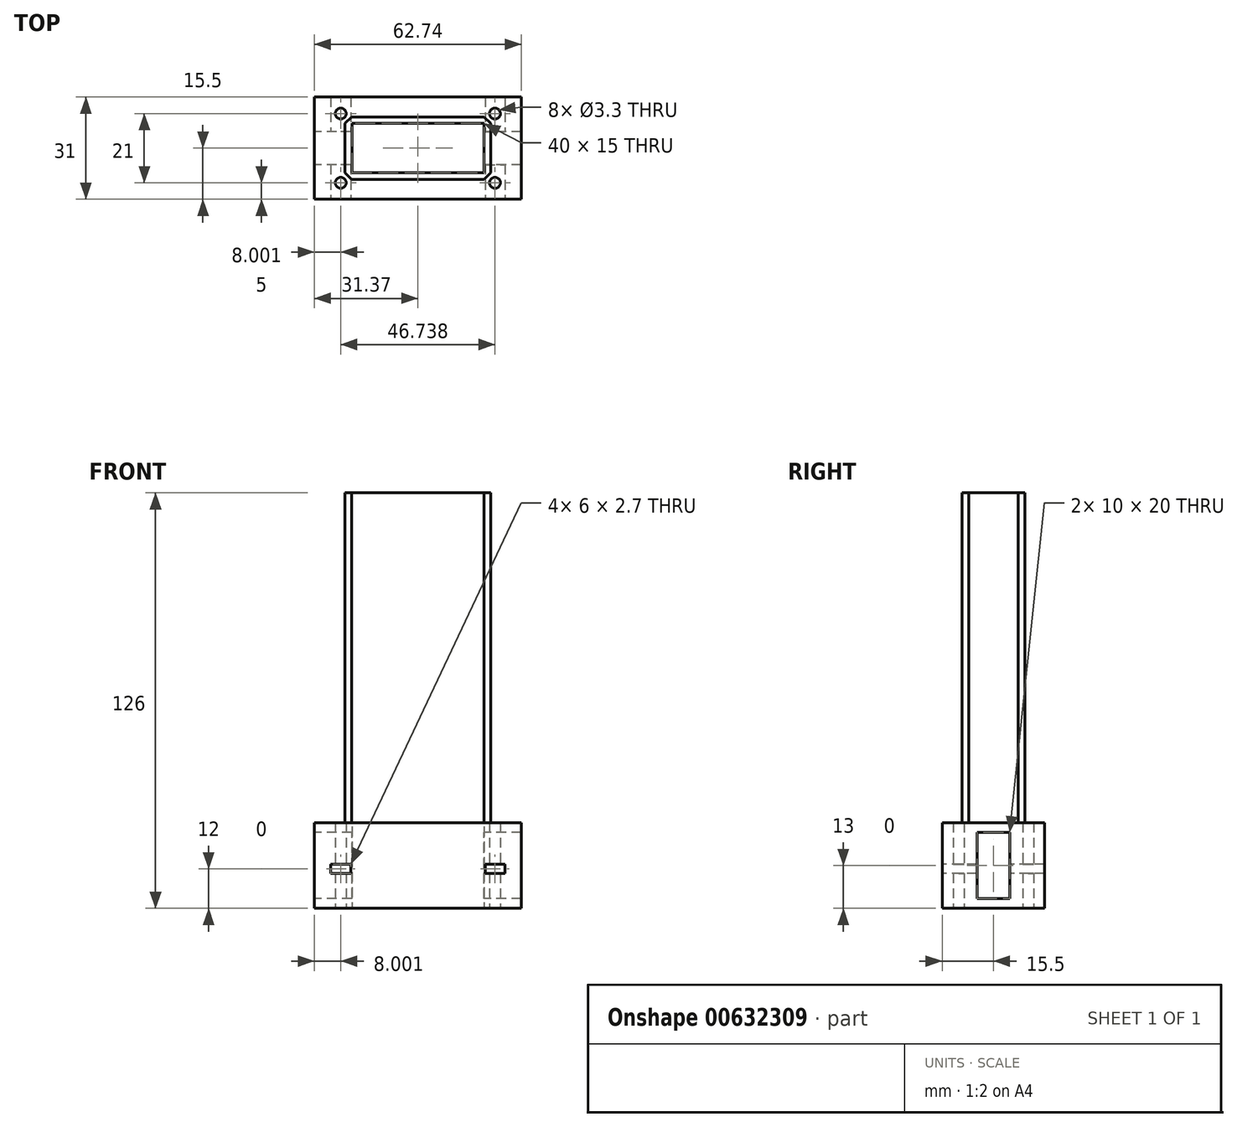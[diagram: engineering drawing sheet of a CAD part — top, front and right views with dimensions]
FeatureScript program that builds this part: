
annotation { "Feature Type Name" : "Feature", "Feature Type Description" : "" }
export const myFeature = defineFeature(function(context is Context, id is Id, definition is map)
    precondition{}
    {
        {
            var Q0;
            Q0=qCreatedBy(makeId("Top.planeOp"),FACE);
            var sketch = newSketch(context, id + "F0", { "sketchPlane" : qUnion([Q0])});
            skLineSegment(sketch, "E0.bottom", {"start": v(31.37, 15.5) * mm, "end": v(-31.37, 15.5) * mm});
            skLineSegment(sketch, "E0.top", {"start": v(31.37, -15.5) * mm, "end": v(-31.37, -15.5) * mm});
            skLineSegment(sketch, "E0.left", {"start": v(31.37, 15.5) * mm, "end": v(31.37, -15.5) * mm});
            skLineSegment(sketch, "E0.right", {"start": v(-31.37, 15.5) * mm, "end": v(-31.37, -15.5) * mm});
            skPoint(sketch, "E0.middle", {"position": v(0, 0) * mm});
            skLineSegment(sketch, "E1.bottom", {"start": v(23.37, -10.5) * mm, "end": v(-23.37, -10.5) * mm, "construction": true});
            skLineSegment(sketch, "E1.top", {"start": v(23.37, 10.5) * mm, "end": v(-23.37, 10.5) * mm, "construction": true});
            skLineSegment(sketch, "E1.left", {"start": v(23.37, -10.5) * mm, "end": v(23.37, 10.5) * mm, "construction": true});
            skLineSegment(sketch, "E1.right", {"start": v(-23.37, -10.5) * mm, "end": v(-23.37, 10.5) * mm, "construction": true});
            skLineSegment(sketch, "E2.bottom", {"start": v(20, -7.5) * mm, "end": v(-20, -7.5) * mm});
            skLineSegment(sketch, "E2.top", {"start": v(20, 7.5) * mm, "end": v(-20, 7.5) * mm});
            skLineSegment(sketch, "E2.left", {"start": v(20, -7.5) * mm, "end": v(20, 7.5) * mm});
            skLineSegment(sketch, "E2.right", {"start": v(-20, -7.5) * mm, "end": v(-20, 7.5) * mm});
            skPoint(sketch, "E3", {"position": v(-23.37, 10.5) * mm});
            skPoint(sketch, "E4", {"position": v(-23.37, -10.5) * mm});
            skPoint(sketch, "E5", {"position": v(23.37, -10.5) * mm});
            skPoint(sketch, "E6", {"position": v(23.37, 10.5) * mm});
            skSolve(sketch);
        }
        {
            var Q0;
            Q0 = qSketchRegion(id + "F0", true);
            extrude(context, id + "F1", {"entities" : qUnion([Q0]), "depth" : 26 * mm, "offsetDistance" : 25 * mm});
        }
        {
            var Q0;
            Q0=makeQuery(id+"F1.opExtrude","SWEPT_FACE",FACE,{"disambiguationData":[OSD([sQuery(id+"F0.wireOp",EDGE,"E0.right")])]});
            var sketch = newSketch(context, id + "F2", { "sketchPlane" : qUnion([Q0])});
            skLineSegment(sketch, "E7.bottom", {"start": v(5, 3) * mm, "end": v(-5, 3) * mm});
            skLineSegment(sketch, "E7.top", {"start": v(5, 23) * mm, "end": v(-5, 23) * mm});
            skLineSegment(sketch, "E7.left", {"start": v(5, 3) * mm, "end": v(5, 23) * mm});
            skLineSegment(sketch, "E7.right", {"start": v(-5, 3) * mm, "end": v(-5, 23) * mm});
            skPoint(sketch, "E7.middle", {"position": v(0, 13) * mm});
            skSolve(sketch);
        }
        {
            var Q0;
            Q0=makeQuery(id+"F2.imprint","IMPRINT",FACE,{"disambiguationData":[TD([[makeQuery(id+"F2.imprint","IMPRINT",EDGE,{"derivedFrom":sQuery(id+"F2.wireOp",EDGE,"E7.bottom")}),-1.0]])]});
            extrude(context, id + "F3", {"entities" : qUnion([Q0]), "operationType" : NewBodyOperationType.REMOVE, "endBound" : BoundingType.THROUGH_ALL, "oppositeDirection" : true, "depth" : 25 * mm, "offsetDistance" : 25 * mm});
        }
        {
            var Q0;
            Q0=sQuery(id+"F0.wireOp",VERTEX,"E3");
            var Q1;
            Q1=sQuery(id+"F0.wireOp",VERTEX,"E4");
            var Q2;
            Q2=sQuery(id+"F0.wireOp",VERTEX,"E5");
            var Q3;
            Q3=sQuery(id+"F0.wireOp",VERTEX,"E6");
            var Q4;
            Q4=makeQuery(id+"F1.opExtrude","SWEPT_BODY",BODY,{"disambiguationData":[OSD([sQuery(id+"F0.wireOp",EDGE,"E0.bottom"),sQuery(id+"F0.wireOp",EDGE,"E0.top"),sQuery(id+"F0.wireOp",EDGE,"E0.left"),sQuery(id+"F0.wireOp",EDGE,"E0.right"),sQuery(id+"F0.wireOp",EDGE,"E2.bottom"),sQuery(id+"F0.wireOp",EDGE,"E2.top"),sQuery(id+"F0.wireOp",EDGE,"E2.left"),sQuery(id+"F0.wireOp",EDGE,"E2.right")])]});
            hole(context, id + "F4", {"style" : HoleStyle.SIMPLE, "endStyle" : HoleEndStyle.THROUGH, "oppositeDirection" : true, "standardTappedOrClearance" : lookupTablePath({ "standard" : "ISO", "fit" : "Normal", "size" : "M3", "type" : "Clearance" }), "standardBlindInLast" : lookupTablePath({ "fit" : "Standard", "standard" : "ISO", "size" : "M3", "type" : "Clearance" }), "holeDiameter" : 3.3 * mm, "majorDiameter" : 5 * mm, "isTappedThrough" : true, "tappedDepth" : 12 * mm, "tapClearance" : 3, "locations" : qUnion([Q0, Q1, Q2, Q3]), "scope" : qUnion([Q4])});
        }
        {
            var Q0;
            Q0=makeQuery(id+"F1.opExtrude","CAP_FACE",FACE,{"disambiguationData":[OSD([sQuery(id+"F0.wireOp",EDGE,"E0.bottom"),sQuery(id+"F0.wireOp",EDGE,"E0.top"),sQuery(id+"F0.wireOp",EDGE,"E0.left"),sQuery(id+"F0.wireOp",EDGE,"E0.right"),sQuery(id+"F0.wireOp",EDGE,"E2.bottom"),sQuery(id+"F0.wireOp",EDGE,"E2.top"),sQuery(id+"F0.wireOp",EDGE,"E2.left"),sQuery(id+"F0.wireOp",EDGE,"E2.right")])],"isStart":false});
            var sketch = newSketch(context, id + "F5", { "sketchPlane" : qUnion([Q0])});
            skLineSegment(sketch, "E8.bottom", {"start": v(-22.06, -9.5) * mm, "end": v(22.06, -9.5) * mm});
            skLineSegment(sketch, "E8.top", {"start": v(-22.06, 9.5) * mm, "end": v(22.06, 9.5) * mm});
            skLineSegment(sketch, "E8.left", {"start": v(-22.06, -9.5) * mm, "end": v(-22.06, 9.5) * mm});
            skLineSegment(sketch, "E8.right", {"start": v(22.06, -9.5) * mm, "end": v(22.06, 9.5) * mm});
            skPoint(sketch, "E8.middle", {"position": v(0, 0) * mm});
            skSolve(sketch);
        }
        {
            var Q0;
            Q0=makeQuery(id+"F5.imprint","IMPRINT",FACE,{"disambiguationData":[TD([[makeQuery(id+"F5.imprint","IMPRINT",EDGE,{"derivedFrom":sQuery(id+"F5.wireOp",EDGE,"E8.bottom")}),1.0]])]});
            extrude(context, id + "F6", {"entities" : qUnion([Q0]), "operationType" : NewBodyOperationType.ADD, "depth" : 100 * mm, "offsetDistance" : 25 * mm});
        }
        {
            var Q0;
            Q0=makeQuery(id+"F6.opExtrude","SWEPT_EDGE",EDGE,{"disambiguationData":[OSD([sQuery(id+"F0.wireOp",EDGE,"E0.bottom"),sQuery(id+"F0.wireOp",EDGE,"E0.top"),sQuery(id+"F0.wireOp",EDGE,"E0.left"),sQuery(id+"F0.wireOp",EDGE,"E0.right"),sQuery(id+"F0.wireOp",EDGE,"E2.bottom"),sQuery(id+"F0.wireOp",EDGE,"E2.top"),sQuery(id+"F0.wireOp",EDGE,"E2.left"),sQuery(id+"F0.wireOp",EDGE,"E2.right"),sQuery(id+"F4.hole-2.sketch.wireOp",EDGE,"core_line_2"),sQuery(id+"F5.wireOp",EDGE,"E8.bottom"),sQuery(id+"F5.wireOp",EDGE,"E8.right")])]});
            var Q1;
            Q1=makeQuery(id+"F6.opExtrude","SWEPT_EDGE",EDGE,{"disambiguationData":[OSD([sQuery(id+"F0.wireOp",EDGE,"E0.bottom"),sQuery(id+"F0.wireOp",EDGE,"E0.top"),sQuery(id+"F0.wireOp",EDGE,"E0.left"),sQuery(id+"F0.wireOp",EDGE,"E0.right"),sQuery(id+"F0.wireOp",EDGE,"E2.bottom"),sQuery(id+"F0.wireOp",EDGE,"E2.top"),sQuery(id+"F0.wireOp",EDGE,"E2.left"),sQuery(id+"F0.wireOp",EDGE,"E2.right"),sQuery(id+"F4.hole-3.sketch.wireOp",EDGE,"core_line_2"),sQuery(id+"F5.wireOp",EDGE,"E8.top"),sQuery(id+"F5.wireOp",EDGE,"E8.right")])]});
            var Q2;
            Q2=makeQuery(id+"F6.opExtrude","SWEPT_EDGE",EDGE,{"disambiguationData":[OSD([sQuery(id+"F0.wireOp",EDGE,"E0.bottom"),sQuery(id+"F0.wireOp",EDGE,"E0.top"),sQuery(id+"F0.wireOp",EDGE,"E0.left"),sQuery(id+"F0.wireOp",EDGE,"E0.right"),sQuery(id+"F0.wireOp",EDGE,"E2.bottom"),sQuery(id+"F0.wireOp",EDGE,"E2.top"),sQuery(id+"F0.wireOp",EDGE,"E2.left"),sQuery(id+"F0.wireOp",EDGE,"E2.right"),sQuery(id+"F4.hole-0.sketch.wireOp",EDGE,"core_line_2"),sQuery(id+"F5.wireOp",EDGE,"E8.top"),sQuery(id+"F5.wireOp",EDGE,"E8.left")])]});
            var Q3;
            Q3=makeQuery(id+"F6.opExtrude","SWEPT_EDGE",EDGE,{"disambiguationData":[OSD([sQuery(id+"F0.wireOp",EDGE,"E0.bottom"),sQuery(id+"F0.wireOp",EDGE,"E0.top"),sQuery(id+"F0.wireOp",EDGE,"E0.left"),sQuery(id+"F0.wireOp",EDGE,"E0.right"),sQuery(id+"F0.wireOp",EDGE,"E2.bottom"),sQuery(id+"F0.wireOp",EDGE,"E2.top"),sQuery(id+"F0.wireOp",EDGE,"E2.left"),sQuery(id+"F0.wireOp",EDGE,"E2.right"),sQuery(id+"F4.hole-1.sketch.wireOp",EDGE,"core_line_2"),sQuery(id+"F5.wireOp",EDGE,"E8.bottom"),sQuery(id+"F5.wireOp",EDGE,"E8.left")])]});
            chamfer(context, id + "F7", {"entities" : qUnion([Q0, Q1, Q2, Q3]), "width" : 2 * mm, "tangentPropagation" : true});
        }
        {
            var Q0;
            Q0=makeQuery(id+"F1.opExtrude","SWEPT_FACE",FACE,{"disambiguationData":[OSD([sQuery(id+"F0.wireOp",EDGE,"E0.top")])]});
            var sketch = newSketch(context, id + "F8", { "sketchPlane" : qUnion([Q0])});
            skLineSegment(sketch, "E9.bottom", {"start": v(-20.37, 10.65) * mm, "end": v(-26.37, 10.65) * mm});
            skLineSegment(sketch, "E9.top", {"start": v(-20.37, 13.35) * mm, "end": v(-26.37, 13.35) * mm});
            skLineSegment(sketch, "E9.left", {"start": v(-20.37, 10.65) * mm, "end": v(-20.37, 13.35) * mm});
            skLineSegment(sketch, "E9.right", {"start": v(-26.37, 10.65) * mm, "end": v(-26.37, 13.35) * mm});
            skPoint(sketch, "E9.middle", {"position": v(-23.37, 12) * mm});
            skLineSegment(sketch, "E10.MirrorCS", {"start": v(20.37, 10.65) * mm, "end": v(26.37, 10.65) * mm});
            skLineSegment(sketch, "E11.MirrorCS", {"start": v(20.37, 13.35) * mm, "end": v(26.37, 13.35) * mm});
            skLineSegment(sketch, "E12.MirrorCS", {"start": v(26.37, 10.65) * mm, "end": v(26.37, 13.35) * mm});
            skLineSegment(sketch, "E13.MirrorCS", {"start": v(20.37, 10.65) * mm, "end": v(20.37, 13.35) * mm});
            skSolve(sketch);
        }
        {
            var Q0;
            Q0=makeQuery(id+"F8.imprint","IMPRINT",FACE,{"disambiguationData":[TD([[makeQuery(id+"F8.imprint","IMPRINT",EDGE,{"derivedFrom":sQuery(id+"F8.wireOp",EDGE,"E9.bottom")}),-1.0]])]});
            var Q1;
            Q1=makeQuery(id+"F8.imprint","IMPRINT",FACE,{"disambiguationData":[TD([[makeQuery(id+"F8.imprint","IMPRINT",EDGE,{"derivedFrom":sQuery(id+"F8.wireOp",EDGE,"E10.MirrorCS")}),1.0]])]});
            extrude(context, id + "F9", {"entities" : qUnion([Q0, Q1]), "operationType" : NewBodyOperationType.REMOVE, "endBound" : BoundingType.THROUGH_ALL, "oppositeDirection" : true, "depth" : 25 * mm, "offsetDistance" : 25 * mm});
        }
    });
